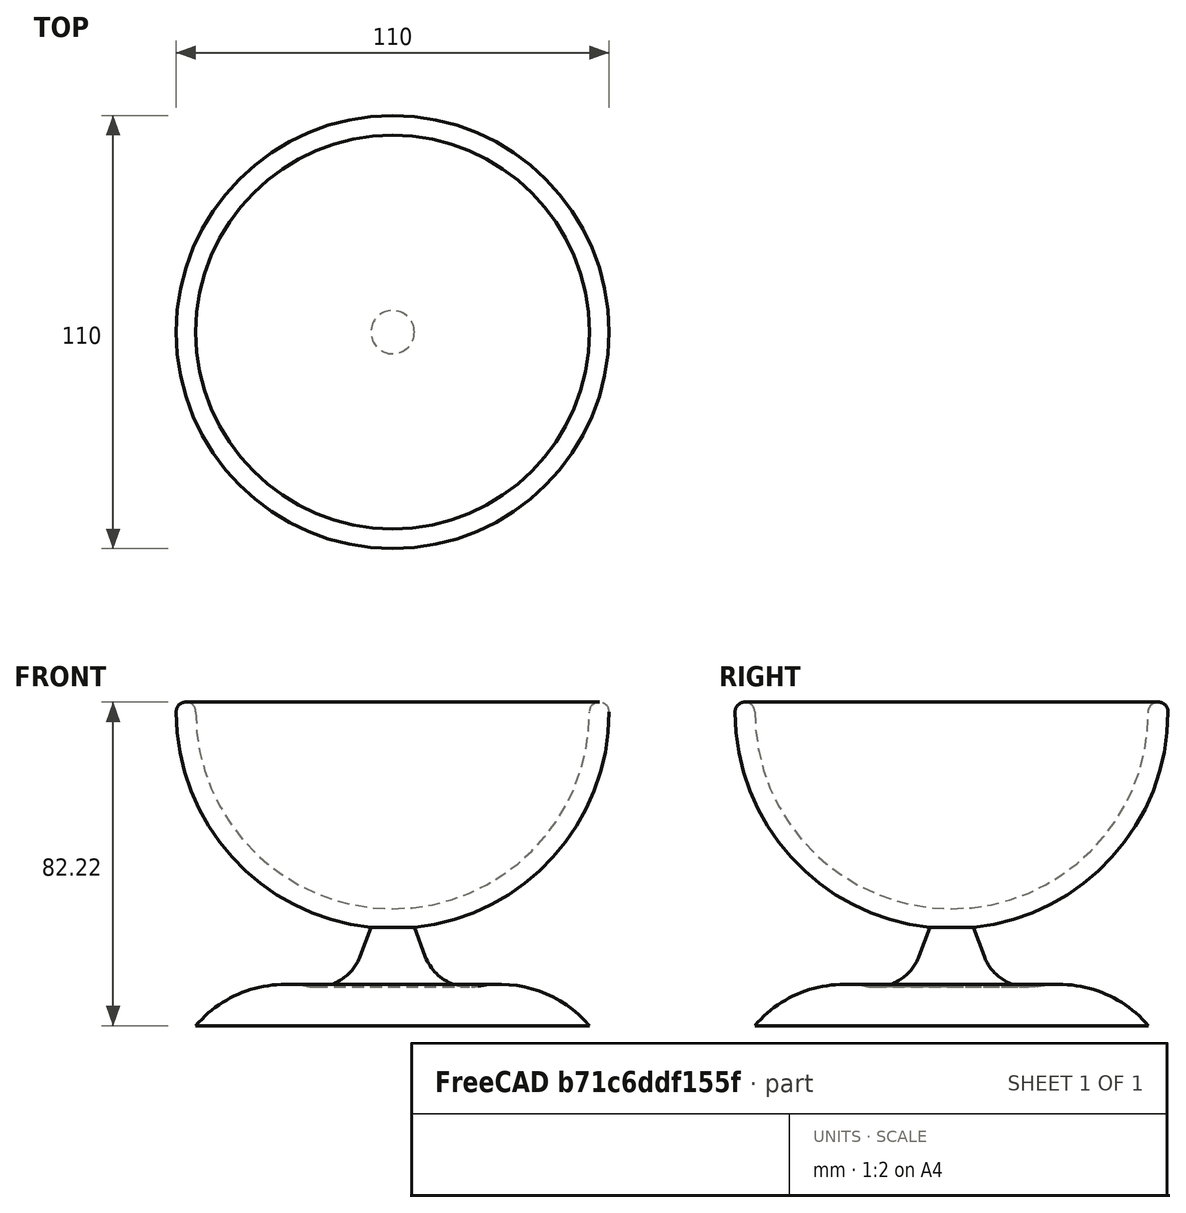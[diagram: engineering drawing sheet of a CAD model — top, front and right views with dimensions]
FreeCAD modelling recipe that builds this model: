
FCSTD DOCUMENT  (FreeCAD 0.19R16203 (Git))
Label: Lathe_1
Comment: by JoshM
License: CreativeCommons Attribution
LicenseURL: http://creativecommons.org/licenses/by/4.0/
objects: Sketcher::SketchObject×1, PartDesign::Revolution×1, PartDesign::Body×1
note: 4 computed .brp shape members not serialized (recipe doc carries the construction recipe); baked Part::Feature solids carry a one-line shape summary decoded from their .brp

FEATURE [Sketcher::SketchObject] Sketch  label="Sketch--Profile"
  MapMode = 5
  Placement = pos=(0,0,0) rot=(1,0,0;1.5708rad)
  Support = -> [XZ_Plane]
  sketch-geometry (8):
    g0: LineSegment StartX=0 StartY=0 StartZ=0 EndX=50 EndY=0 EndZ=0
    g1: LineSegment StartX=0 StartY=0 StartZ=0 EndX=-9.2e-15 EndY=29.7233 EndZ=0
    g2: ArcOfCircle CenterX=27.1976 CenterY=-19.4949 CenterZ=0 NormalX=0 NormalY=0 NormalZ=1 AngleXU=0 Radius=30 StartAngle=0.707361 EndAngle=1.75456
    g3: ArcOfCircle CenterX=19.523 CenterY=21.798 CenterZ=0 NormalX=0 NormalY=0 NormalZ=1 AngleXU=0 Radius=12 StartAngle=3.49989 EndAngle=4.89615
    g4: LineSegment StartX=8.28502 StartY=17.5898 StartZ=0 EndX=5.51023 EndY=25 EndZ=0
    g5: ArcOfCircle CenterX=0 CenterY=79.7233 CenterZ=0 NormalX=0 NormalY=0 NormalZ=1 AngleXU=0 Radius=55 StartAngle=4.81274 EndAngle=6.28319
    g6: ArcOfCircle CenterX=0 CenterY=79.7233 CenterZ=0 NormalX=0 NormalY=0 NormalZ=1 AngleXU=0 Radius=50 StartAngle=4.71239 EndAngle=6.28319
    g7: ArcOfCircle CenterX=52.5 CenterY=79.7233 CenterZ=0 NormalX=0 NormalY=0 NormalZ=1 AngleXU=0 Radius=2.5 StartAngle=-9e-16 EndAngle=3.14159
  constraints (25):
    c: Coincident(g0,g-1)
    c: Horizontal(g0)
    c: DistanceX(g0,g0) = 50
    c: Coincident(g1,g0)
    c: PointOnObject(g1,g-2)
    c: Coincident(g2,g0)
    c: DistanceY(g2) = 10
    c: Angle(g2) = 1.0472
    c: Radius(g2) = 30
    c: Tangent(g3,g2) = 1.5708
    c: Radius(g3) = 12
    c: Angle(g3) = 1.39626
    c: Tangent(g4,g3) = 1.5708
    c: DistanceY(g4) = 25
    c: Coincident(g5,g4)
    c: Horizontal(g5,g5)
    c: PointOnObject(g5,g-2)
    c: DistanceX(g5) = 55
    c: Coincident(g6,g5)
    c: Coincident(g1,g6)
    c: Radius(g6) = 50
    c: Horizontal(g6,g5)
    c: Coincident(g7,g6)
    c: Coincident(g7,g5)
    c: Angle(g7) = 3.14159
FEATURE [PartDesign::Revolution] Revolution
  Angle = 360
  Axis = (-3e-16,3e-16,1)
  Base = (0,0,0)
  Placement = pos=(0,0,0) rot=(1,0,0;1.5708rad)
  Profile = -> Sketch
  ReferenceAxis = -> Z_Axis
  Refine = true
  Reversed = true
FEATURE [PartDesign::Body] Body  label="Lathe_1"
  Group = -> [Sketch,Revolution]
  Origin = -> Origin
  Tip = -> Revolution
